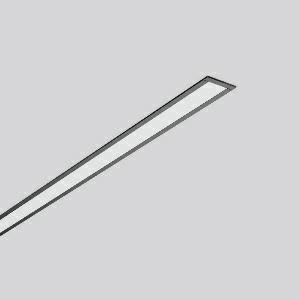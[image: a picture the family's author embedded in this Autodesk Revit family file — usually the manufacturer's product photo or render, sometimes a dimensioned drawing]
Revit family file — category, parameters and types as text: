
# Revit family: less_is_more_27_312178_003_6e80
name_source: partatom
category: Lighting Fixtures
units: mm (PartAtom-declared; Revit-internal decimal feet)

## family parameters
Cut with Voids When Loaded = No
Host = Face
Light Source = No
Part Type = Normal
Room Calculation Point = No
Round Connector Dimension = Use Diameter
Shared = No

## types (1)
- LESS IS MORE 27 (1 x LED Modul 830, 2400 lm, 3000)
    Apparent Load = 43 VA
    CIE Flux Codes = 48 79 96 100 100
    Color Rendering = 80
    Color Temperature = 3000
    Default Elevation = 1800 mm
    Description = Series: LESS IS MORE 27
Recessed ceiling and wall luminaire with slim design. Housing: extruded aluminium profile, powder-coated. End cap aluminium powder-coated. Diffuser made of non-yellowing plastic (PMMA), opal. Suitable for Recessed ceiling mounting, wall (recessed). External driver with connecting cable. 
Colour: deep black, matt (RAL 9005)
Length: 1514 mm
Width: 38 mm
Height: 2 mm
Cut-out length: 1506 mm
Cut-out width: 30 mm
Recess height: 45-60 mm
Luminaire: recess height: 37 mm
Lamp: LED
Socket: without socket
Colour temperature: 3000K
Colour rendering index (CRI): 82
System power: 43 W
Rated luminous flux: 2400 lm
Luminous efficiency: 56 lm/W
Control gear: Regulated power supply
Protection class: II
Type of protection: IP 20
    Height = 0 mm  [stored 0 ft]
    Lamp = 1 x LED Modul 830
    Lamp Light Flux = 2400 lm
    Lamp count = 1
    Length = 1514 mm
    Lifetime = 50000 h
    Luminous efficacy = 56 lm/W
    Manufacturer = RZB
    ModVariant = No
    Model = 312178.003
    Mounting Place = Ceiling, Wall
    Mounting Type = Recessed
    Number of Poles = 1
    OnlyDefault = Yes
    Power Factor = 1
    Product Name = LESS IS MORE 27
    Product group = Recessed LED linear luminaires
    ProductGroupID = 407
    Protection Class = Protection class II
    Protection Degree = IP 20
    RLX_Detail_Level = 1
    RLX_Emergency_Light_Flux = 0 lm
    RLX_Emergency_Type = 0
    RLX_Emergency_Type_DB = No
    RlxData = <blob elided: 26165 chars, md5=9cda8dfa>
    Socket = socket
    Standby Power = 0 W
    System Light Flux = 2400 lm
    System Power = 43 W
    Type Comments = Product without accessories
    Type Image = 312176.003.jpg
    URL = http://relux.com
    VarID = ---
    Voltage = 230 V
    Voltage Range = 220-240 V
    Weight = 0.00 kg
    Width = 38 mm

note: [stored X ft] marks values corroborated as IEEE doubles in the binary element streams (Revit-internal decimal feet)

## geometry (parser evidence)
native form markers: Blend x4, Sweep x11
no freeform markers — native parametric forms only
